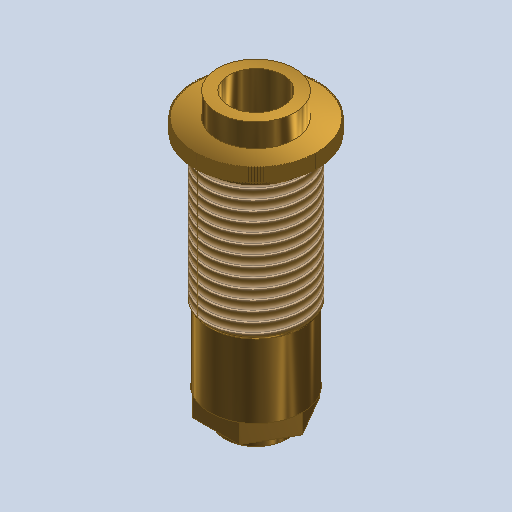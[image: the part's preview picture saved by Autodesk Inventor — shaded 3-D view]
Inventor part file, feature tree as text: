
AUTODESK INVENTOR PART (.ipt)
format: ipt  version: 2023 (Build 270158030, 158C)  size: 1,382,400 bytes
history: native  units: mm
features: extrude x11, sketch x11, other x1, fillet x1, thread x1, projected_geometry x1
ambient origin geometry x8: Origin, YZ Plane, XZ Plane, XY Plane, X Axis, Y Axis, Z Axis, Center Point
bodies: Body1 (feature_tree)
feature tree (26):
  other  "ソリッド1"
  extrude  "押し出し1"  Depth=11.0mm
  extrude  "押し出し2"  Depth=2.5mm TaperAngle=0.0deg
  extrude  "押し出し3"  Depth=12.0mm
  extrude  "押し出し4"  Depth=9.5mm TaperAngle=0.0deg
  extrude  "押し出し5"  Depth=12.5mm
  extrude  "押し出し6"  Depth=18.95mm TaperAngle=0.0deg
  extrude  "押し出し7"  Depth=16.0mm
  extrude  "押し出し8"  Depth=1.75mm TaperAngle=0.0deg
  extrude  "押し出し9"  Depth=2.5mm TaperAngle=0.0deg
  extrude  "押し出し11"  Depth=2.5mm TaperAngle=0.0deg
  extrude  "押し出し12"  Depth=7.0mm
  fillet  "フィレット1"  Radius=7.0mm
  thread  "ねじ5"
  sketch  "スケッチ1"
  sketch  "スケッチ2"
  sketch  "スケッチ3"
  sketch  "スケッチ4"
  sketch  "スケッチ5"
  sketch  "スケッチ6"
  projected_geometry  "投影ループ1"
  sketch  "スケッチ8"
  sketch  "スケッチ9"
  sketch  "スケッチ11"
  sketch  "スケッチ12"
  sketch  "スケッチ13"
